# Revit family: NSAL_приток
name_source: partatom
category: Воздухораспределители
revit_build: Autodesk Revit 2014 (Build: 20130308_1515(x64)
units: mm (PartAtom-declared; Revit-internal decimal feet)

## types (144) — shared parameters
1 секция = Да
Offset = 15 мм
T' = 20 мм
URL = http://inplast.ru
Изготовитель = INPLAST-SMAY
Материал = Алюминий_аннодированный (INPLAST)
Рамка_T' = 3 мм
zero-valued in all types: Вес, кг

## per-type parameters (varying)
| type | 2 секция | 3 секция | 4 секция | Aef | L' | W1 | W2 | Вид диффузора | Количество щелей | Описание | Рамка верх | Рамка низ | Тип крепежа |
| NSAL-1-500-0-0-АА | Нет | Нет | Нет | 0.008 м² | 500 мм | 27 мм | 27 мм | единичная установка | 1 | Приточный диффузор однощелевой. Исполнение - алюминий анодированный | Да | Да | с помощью консоли |
| NSAL-2-500-0-0-AA | Да | Нет | Нет | 0.015 м² | 500 мм | 52 мм | 26 мм | единичная установка | 2 | Приточный диффузор двухщелевой. Исполнение - алюминий анодированный | Да | Да | с помощью консоли |
| NSAL-3-500-0-0-AA | Да | Да | Нет | 0.023 м² | 500 мм | 76 мм | 25 мм | единичная установка | 3 | Приточный диффузор трехщелевой. Исполнение - алюминий анодированный | Да | Да | с помощью консоли |
| NSAL-4-500-0-0-AA | Да | Да | Да | 0.030 м² | 500 мм | 101 мм | 25 мм | единичная установка | 4 | Приточный диффузор четырехщелевой. Исполнение - алюминий анодированный | Да | Да | с помощью консоли |
| NSAL-1-500-SK-0-AA | Нет | Нет | Нет | 0.008 м² | 500 мм | 27 мм | 27 мм | крайний элемент | 1 | Приточный диффузор однощелевой. Исполнение - алюминий анодированный | Да | Нет | с помощью консоли |
| NSAL-2-500-SK-0-AA | Да | Нет | Нет | 0.015 м² | 500 мм | 52 мм | 26 мм | крайний элемент | 2 | Приточный диффузор двухщелевой. Исполнение - алюминий анодированный | Да | Нет | с помощью консоли |
| NSAL-3-500-SK-0-AA | Да | Да | Нет | 0.023 м² | 500 мм | 76 мм | 25 мм | крайний элемент | 3 | Приточный диффузор трехщелевой. Исполнение - алюминий анодированный | Да | Нет | с помощью консоли |
| NSAL-4-500-SK-0-AA | Да | Да | Да | 0.030 м² | 500 мм | 101 мм | 25 мм | крайний элемент | 4 | Приточный диффузор четырехщелевой. Исполнение - алюминий анодированный | Да | Нет | с помощью консоли |
| NSAL-1-500-WN-0-AA | Нет | Нет | Нет | 0.008 м² | 500 мм | 27 мм | 27 мм | внутренний элемент | 1 | Приточный диффузор однощелевой. Исполнение - алюминий анодированный | Нет | Нет | с помощью консоли |
| NSAL-2-500-WN-0-AA | Да | Нет | Нет | 0.015 м² | 500 мм | 52 мм | 26 мм | внутренний элемент | 2 | Приточный диффузор двухщелевой. Исполнение - алюминий анодированный | Нет | Нет | с помощью консоли |
| NSAL-3-500-WN-0-AA | Да | Да | Нет | 0.023 м² | 500 мм | 76 мм | 25 мм | внутренний элемент | 3 | Приточный диффузор трехщелевой. Исполнение - алюминий анодированный | Нет | Нет | с помощью консоли |
| NSAL-4-500-WN-0-AA | Да | Да | Да | 0.030 м² | 500 мм | 101 мм | 25 мм | внутренний элемент | 4 | Приточный диффузор четырехщелевой. Исполнение - алюминий анодированный | Нет | Нет | с помощью консоли |
| NSAL-1-500-0-WK-AA | Нет | Нет | Нет | 0.008 м² | 500 мм | 27 мм | 27 мм | единичная установка | 1 | Приточный диффузор однощелевой. Исполнение - алюминий анодированный | Да | Да | с помощью саморезов |
| NSAL-2-500-0-WK-AA | Да | Нет | Нет | 0.015 м² | 500 мм | 52 мм | 26 мм | единичная установка | 2 | Приточный диффузор двухщелевой. Исполнение - алюминий анодированный | Да | Да | с помощью саморезов |
| NSAL-3-500-0-WK-AA | Да | Да | Нет | 0.023 м² | 500 мм | 76 мм | 25 мм | единичная установка | 3 | Приточный диффузор трехщелевой. Исполнение - алюминий анодированный | Да | Да | с помощью саморезов |
| NSAL-4-500-0-WK-AA | Да | Да | Да | 0.030 м² | 500 мм | 101 мм | 25 мм | единичная установка | 4 | Приточный диффузор четырехщелевой. Исполнение - алюминий анодированный | Да | Да | с помощью саморезов |
| NSAL-1-500-SK-WK-AA | Нет | Нет | Нет | 0.008 м² | 500 мм | 27 мм | 27 мм | крайний элемент | 1 | Приточный диффузор однощелевой. Исполнение - алюминий анодированный | Да | Нет | с помощью саморезов |
| NSAL-2-500-SK-WK-AA | Да | Нет | Нет | 0.015 м² | 500 мм | 52 мм | 26 мм | крайний элемент | 2 | Приточный диффузор двухщелевой. Исполнение - алюминий анодированный | Да | Нет | с помощью саморезов |
| NSAL-3-500-SK-WK-AA | Да | Да | Нет | 0.023 м² | 500 мм | 76 мм | 25 мм | крайний элемент | 3 | Приточный диффузор трехщелевой. Исполнение - алюминий анодированный | Да | Нет | с помощью саморезов |
| NSAL-4-500-SK-WK-AA | Да | Да | Да | 0.030 м² | 500 мм | 101 мм | 25 мм | крайний элемент | 4 | Приточный диффузор четырехщелевой. Исполнение - алюминий анодированный | Да | Нет | с помощью саморезов |
| NSAL-1-500-WN-WK-AA | Нет | Нет | Нет | 0.008 м² | 500 мм | 27 мм | 27 мм | внутренний элемент | 1 | Приточный диффузор однощелевой. Исполнение - алюминий анодированный | Нет | Нет | с помощью саморезов |
| NSAL-2-500-WN-WK-AA | Да | Нет | Нет | 0.015 м² | 500 мм | 52 мм | 26 мм | внутренний элемент | 2 | Приточный диффузор двухщелевой. Исполнение - алюминий анодированный | Нет | Нет | с помощью саморезов |
| NSAL-3-500-WN-WK-AA | Да | Да | Нет | 0.023 м² | 500 мм | 76 мм | 25 мм | внутренний элемент | 3 | Приточный диффузор трехщелевой. Исполнение - алюминий анодированный | Нет | Нет | с помощью саморезов |
| NSAL-4-500-WN-WK-AA | Да | Да | Да | 0.030 м² | 500 мм | 101 мм | 25 мм | внутренний элемент | 4 | Приточный диффузор четырехщелевой. Исполнение - алюминий анодированный | Нет | Нет | с помощью саморезов |
| NSAL-1-800-0-0-AA | Нет | Нет | Нет | 0.013 м² | 800 мм | 27 мм | 27 мм | единичная установка | 1 | Приточный диффузор однощелевой. Исполнение - алюминий анодированный | Да | Да | с помощью консоли |
| NSAL-2-800-0-0-AA | Да | Нет | Нет | 0.025 м² | 800 мм | 52 мм | 26 мм | единичная установка | 2 | Приточный диффузор двухщелевой. Исполнение - алюминий анодированный | Да | Да | с помощью консоли |
| NSAL-3-800-0-0-AA | Да | Да | Нет | 0.037 м² | 800 мм | 76 мм | 25 мм | единичная установка | 3 | Приточный диффузор трехщелевой. Исполнение - алюминий анодированный | Да | Да | с помощью консоли |
| NSAL-4-800-0-0-AA | Да | Да | Да | 0.049 м² | 800 мм | 101 мм | 25 мм | единичная установка | 4 | Приточный диффузор четырехщелевой. Исполнение - алюминий анодированный | Да | Да | с помощью консоли |
| NSAL-1-800-SK-0-AA | Нет | Нет | Нет | 0.013 м² | 800 мм | 27 мм | 27 мм | крайний элемент | 1 | Приточный диффузор однощелевой. Исполнение - алюминий анодированный | Да | Нет | с помощью консоли |
| NSAL-2-800-SK-0-AA | Да | Нет | Нет | 0.025 м² | 800 мм | 52 мм | 26 мм | крайний элемент | 2 | Приточный диффузор двухщелевой. Исполнение - алюминий анодированный | Да | Нет | с помощью консоли |
| NSAL-3-800-SK-0-AA | Да | Да | Нет | 0.037 м² | 800 мм | 76 мм | 25 мм | крайний элемент | 3 | Приточный диффузор трехщелевой. Исполнение - алюминий анодированный | Да | Нет | с помощью консоли |
| NSAL-4-800-SK-0-AA | Да | Да | Да | 0.049 м² | 800 мм | 101 мм | 25 мм | крайний элемент | 4 | Приточный диффузор четырехщелевой. Исполнение - алюминий анодированный | Да | Нет | с помощью консоли |
| NSAL-1-800-WN-0-AA | Нет | Нет | Нет | 0.013 м² | 800 мм | 27 мм | 27 мм | внутренний элемент | 1 | Приточный диффузор однощелевой. Исполнение - алюминий анодированный | Нет | Нет | с помощью консоли |
| NSAL-2-800-WN-0-AA | Да | Нет | Нет | 0.025 м² | 800 мм | 52 мм | 26 мм | внутренний элемент | 2 | Приточный диффузор двухщелевой. Исполнение - алюминий анодированный | Нет | Нет | с помощью консоли |
| NSAL-3-800-WN-0-AA | Да | Да | Нет | 0.037 м² | 800 мм | 76 мм | 25 мм | внутренний элемент | 3 | Приточный диффузор трехщелевой. Исполнение - алюминий анодированный | Нет | Нет | с помощью консоли |
| NSAL-4-800-WN-0-AA | Да | Да | Да | 0.049 м² | 800 мм | 101 мм | 25 мм | внутренний элемент | 4 | Приточный диффузор четырехщелевой. Исполнение - алюминий анодированный | Нет | Нет | с помощью консоли |
| NSAL-1-800-0-WK-AA | Нет | Нет | Нет | 0.013 м² | 800 мм | 27 мм | 27 мм | единичная установка | 1 | Приточный диффузор однощелевой. Исполнение - алюминий анодированный | Да | Да | с помощью саморезов |
| NSAL-2-800-0-WK-AA | Да | Нет | Нет | 0.025 м² | 800 мм | 52 мм | 26 мм | единичная установка | 2 | Приточный диффузор двухщелевой. Исполнение - алюминий анодированный | Да | Да | с помощью саморезов |
| NSAL-3-800-0-WK-AA | Да | Да | Нет | 0.037 м² | 800 мм | 76 мм | 25 мм | единичная установка | 3 | Приточный диффузор трехщелевой. Исполнение - алюминий анодированный | Да | Да | с помощью саморезов |
| NSAL-4-800-0-WK-AA | Да | Да | Да | 0.049 м² | 800 мм | 101 мм | 25 мм | единичная установка | 4 | Приточный диффузор четырехщелевой. Исполнение - алюминий анодированный | Да | Да | с помощью саморезов |
| NSAL-1-800-SK-WK-AA | Нет | Нет | Нет | 0.013 м² | 800 мм | 27 мм | 27 мм | крайний элемент | 1 | Приточный диффузор однощелевой. Исполнение - алюминий анодированный | Да | Нет | с помощью саморезов |
| NSAL-2-800-SK-WK-AA | Да | Нет | Нет | 0.025 м² | 800 мм | 52 мм | 26 мм | крайний элемент | 2 | Приточный диффузор двухщелевой. Исполнение - алюминий анодированный | Да | Нет | с помощью саморезов |
| NSAL-3-800-SK-WK-AA | Да | Да | Нет | 0.037 м² | 800 мм | 76 мм | 25 мм | крайний элемент | 3 | Приточный диффузор трехщелевой. Исполнение - алюминий анодированный | Да | Нет | с помощью саморезов |
| NSAL-4-800-SK-WK-AA | Да | Да | Да | 0.049 м² | 800 мм | 101 мм | 25 мм | крайний элемент | 4 | Приточный диффузор четырехщелевой. Исполнение - алюминий анодированный | Да | Нет | с помощью саморезов |
| NSAL-1-800-WN-WK-AA | Нет | Нет | Нет | 0.013 м² | 800 мм | 27 мм | 27 мм | внутренний элемент | 1 | Приточный диффузор однощелевой. Исполнение - алюминий анодированный | Нет | Нет | с помощью саморезов |
| NSAL-2-800-WN-WK-AA | Да | Нет | Нет | 0.025 м² | 800 мм | 52 мм | 26 мм | внутренний элемент | 2 | Приточный диффузор двухщелевой. Исполнение - алюминий анодированный | Нет | Нет | с помощью саморезов |
| NSAL-3-800-WN-WK-AA | Да | Да | Нет | 0.037 м² | 800 мм | 76 мм | 25 мм | внутренний элемент | 3 | Приточный диффузор трехщелевой. Исполнение - алюминий анодированный | Нет | Нет | с помощью саморезов |
| NSAL-4-800-WN-WK-AA | Да | Да | Да | 0.049 м² | 800 мм | 101 мм | 25 мм | внутренний элемент | 4 | Приточный диффузор четырехщелевой. Исполнение - алюминий анодированный | Нет | Нет | с помощью саморезов |
| NSAL-1-1000-0-0-AA | Нет | Нет | Нет | 0.016 м² | 1000 мм | 27 мм | 27 мм | единичная установка | 1 | Приточный диффузор однощелевой. Исполнение - алюминий анодированный | Да | Да | с помощью консоли |
| NSAL-2-1000-0-0-AA | Да | Нет | Нет | 0.031 м² | 1000 мм | 52 мм | 26 мм | единичная установка | 2 | Приточный диффузор двухщелевой. Исполнение - алюминий анодированный | Да | Да | с помощью консоли |
| NSAL-3-1000-0-0-AA | Да | Да | Нет | 0.046 м² | 1000 мм | 76 мм | 25 мм | единичная установка | 3 | Приточный диффузор трехщелевой. Исполнение - алюминий анодированный | Да | Да | с помощью консоли |
| NSAL-4-1000-0-0-AA | Да | Да | Да | 0.061 м² | 1000 мм | 101 мм | 25 мм | единичная установка | 4 | Приточный диффузор четырехщелевой. Исполнение - алюминий анодированный | Да | Да | с помощью консоли |
| NSAL-1-1000-SK-0-AA | Нет | Нет | Нет | 0.016 м² | 1000 мм | 27 мм | 27 мм | крайний элемент | 1 | Приточный диффузор однощелевой. Исполнение - алюминий анодированный | Да | Нет | с помощью консоли |
| NSAL-2-1000-SK-0-AA | Да | Нет | Нет | 0.031 м² | 1000 мм | 52 мм | 26 мм | крайний элемент | 2 | Приточный диффузор двухщелевой. Исполнение - алюминий анодированный | Да | Нет | с помощью консоли |
| NSAL-3-1000-SK-0-AA | Да | Да | Нет | 0.046 м² | 1000 мм | 76 мм | 25 мм | крайний элемент | 3 | Приточный диффузор трехщелевой. Исполнение - алюминий анодированный | Да | Нет | с помощью консоли |
| NSAL-4-1000-SK-0-AA | Да | Да | Да | 0.061 м² | 1000 мм | 101 мм | 25 мм | крайний элемент | 4 | Приточный диффузор четырехщелевой. Исполнение - алюминий анодированный | Да | Нет | с помощью консоли |
| NSAL-1-1000-WN-0-AA | Нет | Нет | Нет | 0.016 м² | 1000 мм | 27 мм | 27 мм | внутренний элемент | 1 | Приточный диффузор однощелевой. Исполнение - алюминий анодированный | Нет | Нет | с помощью консоли |
| NSAL-2-1000-WN-0-AA | Да | Нет | Нет | 0.031 м² | 1000 мм | 52 мм | 26 мм | внутренний элемент | 2 | Приточный диффузор двухщелевой. Исполнение - алюминий анодированный | Нет | Нет | с помощью консоли |
| NSAL-3-1000-WN-0-AA | Да | Да | Нет | 0.046 м² | 1000 мм | 76 мм | 25 мм | внутренний элемент | 3 | Приточный диффузор трехщелевой. Исполнение - алюминий анодированный | Нет | Нет | с помощью консоли |
| NSAL-4-1000-WN-0-AA | Да | Да | Да | 0.061 м² | 1000 мм | 101 мм | 25 мм | внутренний элемент | 4 | Приточный диффузор четырехщелевой. Исполнение - алюминий анодированный | Нет | Нет | с помощью консоли |
| NSAL-1-1000-0-WK-AA | Нет | Нет | Нет | 0.016 м² | 1000 мм | 27 мм | 27 мм | единичная установка | 1 | Приточный диффузор однощелевой. Исполнение - алюминий анодированный | Да | Да | с помощью саморезов |
| NSAL-2-1000-0-WK-AA | Да | Нет | Нет | 0.031 м² | 1000 мм | 52 мм | 26 мм | единичная установка | 2 | Приточный диффузор двухщелевой. Исполнение - алюминий анодированный | Да | Да | с помощью саморезов |
| NSAL-3-1000-0-WK-AA | Да | Да | Нет | 0.046 м² | 1000 мм | 76 мм | 25 мм | единичная установка | 3 | Приточный диффузор трехщелевой. Исполнение - алюминий анодированный | Да | Да | с помощью саморезов |
| NSAL-4-1000-0-WK-AA | Да | Да | Да | 0.061 м² | 1000 мм | 101 мм | 25 мм | единичная установка | 4 | Приточный диффузор четырехщелевой. Исполнение - алюминий анодированный | Да | Да | с помощью саморезов |
| NSAL-1-1000-SK-WK-AA | Нет | Нет | Нет | 0.016 м² | 1000 мм | 27 мм | 27 мм | крайний элемент | 1 | Приточный диффузор однощелевой. Исполнение - алюминий анодированный | Да | Нет | с помощью саморезов |
| NSAL-2-1000-SK-WK-AA | Да | Нет | Нет | 0.031 м² | 1000 мм | 52 мм | 26 мм | крайний элемент | 2 | Приточный диффузор двухщелевой. Исполнение - алюминий анодированный | Да | Нет | с помощью саморезов |
| NSAL-3-1000-SK-WK-AA | Да | Да | Нет | 0.046 м² | 1000 мм | 76 мм | 25 мм | крайний элемент | 3 | Приточный диффузор трехщелевой. Исполнение - алюминий анодированный | Да | Нет | с помощью саморезов |
| NSAL-4-1000-SK-WK-AA | Да | Да | Да | 0.061 м² | 1000 мм | 101 мм | 25 мм | крайний элемент | 4 | Приточный диффузор четырехщелевой. Исполнение - алюминий анодированный | Да | Нет | с помощью саморезов |
| NSAL-1-1000-WN-WK-AA | Нет | Нет | Нет | 0.016 м² | 1000 мм | 27 мм | 27 мм | внутренний элемент | 1 | Приточный диффузор однощелевой. Исполнение - алюминий анодированный | Нет | Нет | с помощью саморезов |
| NSAL-2-1000-WN-WK-AA | Да | Нет | Нет | 0.031 м² | 1000 мм | 52 мм | 26 мм | внутренний элемент | 2 | Приточный диффузор двухщелевой. Исполнение - алюминий анодированный | Нет | Нет | с помощью саморезов |
| NSAL-3-1000-WN-WK-AA | Да | Да | Нет | 0.046 м² | 1000 мм | 76 мм | 25 мм | внутренний элемент | 3 | Приточный диффузор трехщелевой. Исполнение - алюминий анодированный | Нет | Нет | с помощью саморезов |
| NSAL-4-1000-WN-WK-AA | Да | Да | Да | 0.061 м² | 1000 мм | 101 мм | 25 мм | внутренний элемент | 4 | Приточный диффузор четырехщелевой. Исполнение - алюминий анодированный | Нет | Нет | с помощью саморезов |
| NSAL-1-1200-0-0-AA | Нет | Нет | Нет | 0.019 м² | 1200 мм | 27 мм | 27 мм | единичная установка | 1 | Приточный диффузор однощелевой. Исполнение - алюминий анодированный | Да | Да | с помощью консоли |
| NSAL-2-1200-0-0-AA | Да | Нет | Нет | 0.037 м² | 1200 мм | 52 мм | 26 мм | единичная установка | 2 | Приточный диффузор двухщелевой. Исполнение - алюминий анодированный | Да | Да | с помощью консоли |
| NSAL-3-1200-0-0-AA | Да | Да | Нет | 0.055 м² | 1200 мм | 76 мм | 25 мм | единичная установка | 3 | Приточный диффузор трехщелевой. Исполнение - алюминий анодированный | Да | Да | с помощью консоли |
| NSAL-4-1200-0-0-AA | Да | Да | Да | 0.073 м² | 1200 мм | 101 мм | 25 мм | единичная установка | 4 | Приточный диффузор четырехщелевой. Исполнение - алюминий анодированный | Да | Да | с помощью консоли |
| NSAL-1-1200-SK-0-AA | Нет | Нет | Нет | 0.019 м² | 1200 мм | 27 мм | 27 мм | крайний элемент | 1 | Приточный диффузор однощелевой. Исполнение - алюминий анодированный | Да | Нет | с помощью консоли |
| NSAL-2-1200-SK-0-AA | Да | Нет | Нет | 0.037 м² | 1200 мм | 52 мм | 26 мм | крайний элемент | 2 | Приточный диффузор двухщелевой. Исполнение - алюминий анодированный | Да | Нет | с помощью консоли |
| NSAL-3-1200-SK-0-AA | Да | Да | Нет | 0.055 м² | 1200 мм | 76 мм | 25 мм | крайний элемент | 3 | Приточный диффузор трехщелевой. Исполнение - алюминий анодированный | Да | Нет | с помощью консоли |
| NSAL-4-1200-SK-0-AA | Да | Да | Да | 0.073 м² | 1200 мм | 101 мм | 25 мм | крайний элемент | 4 | Приточный диффузор четырехщелевой. Исполнение - алюминий анодированный | Да | Нет | с помощью консоли |
| NSAL-1-1200-WN-0-AA | Нет | Нет | Нет | 0.019 м² | 1200 мм | 27 мм | 27 мм | внутренний элемент | 1 | Приточный диффузор однощелевой. Исполнение - алюминий анодированный | Нет | Нет | с помощью консоли |
| NSAL-2-1200-WN-0-AA | Да | Нет | Нет | 0.037 м² | 1200 мм | 52 мм | 26 мм | внутренний элемент | 2 | Приточный диффузор двухщелевой. Исполнение - алюминий анодированный | Нет | Нет | с помощью консоли |
| NSAL-3-1200-WN-0-AA | Да | Да | Нет | 0.055 м² | 1200 мм | 76 мм | 25 мм | внутренний элемент | 3 | Приточный диффузор трехщелевой. Исполнение - алюминий анодированный | Нет | Нет | с помощью консоли |
| NSAL-4-1200-WN-0-AA | Да | Да | Да | 0.073 м² | 1200 мм | 101 мм | 25 мм | внутренний элемент | 4 | Приточный диффузор четырехщелевой. Исполнение - алюминий анодированный | Нет | Нет | с помощью консоли |
| NSAL-1-1200-0-WK-AA | Нет | Нет | Нет | 0.019 м² | 1200 мм | 27 мм | 27 мм | единичная установка | 1 | Приточный диффузор однощелевой. Исполнение - алюминий анодированный | Да | Да | с помощью саморезов |
| NSAL-2-1200-0-WK-AA | Да | Нет | Нет | 0.037 м² | 1200 мм | 52 мм | 26 мм | единичная установка | 2 | Приточный диффузор двухщелевой. Исполнение - алюминий анодированный | Да | Да | с помощью саморезов |
| NSAL-3-1200-0-WK-AA | Да | Да | Нет | 0.055 м² | 1200 мм | 76 мм | 25 мм | единичная установка | 3 | Приточный диффузор трехщелевой. Исполнение - алюминий анодированный | Да | Да | с помощью саморезов |
| NSAL-4-1200-0-WK-AA | Да | Да | Да | 0.073 м² | 1200 мм | 101 мм | 25 мм | единичная установка | 4 | Приточный диффузор четырехщелевой. Исполнение - алюминий анодированный | Да | Да | с помощью саморезов |
| NSAL-1-1200-SK-WK-AA | Нет | Нет | Нет | 0.019 м² | 1200 мм | 27 мм | 27 мм | крайний элемент | 1 | Приточный диффузор однощелевой. Исполнение - алюминий анодированный | Да | Нет | с помощью саморезов |
| NSAL-2-1200-SK-WK-AA | Да | Нет | Нет | 0.037 м² | 1200 мм | 52 мм | 26 мм | крайний элемент | 2 | Приточный диффузор двухщелевой. Исполнение - алюминий анодированный | Да | Нет | с помощью саморезов |
| NSAL-3-1200-SK-WK-AA | Да | Да | Нет | 0.055 м² | 1200 мм | 76 мм | 25 мм | крайний элемент | 3 | Приточный диффузор трехщелевой. Исполнение - алюминий анодированный | Да | Нет | с помощью саморезов |
| NSAL-4-1200-SK-WK-AA | Да | Да | Да | 0.073 м² | 1200 мм | 101 мм | 25 мм | крайний элемент | 4 | Приточный диффузор четырехщелевой. Исполнение - алюминий анодированный | Да | Нет | с помощью саморезов |
| NSAL-1-1200-WN-WK-AA | Нет | Нет | Нет | 0.019 м² | 1200 мм | 27 мм | 27 мм | внутренний элемент | 1 | Приточный диффузор однощелевой. Исполнение - алюминий анодированный | Нет | Нет | с помощью саморезов |
| NSAL-2-1200-WN-WK-AA | Да | Нет | Нет | 0.037 м² | 1200 мм | 52 мм | 26 мм | внутренний элемент | 2 | Приточный диффузор двухщелевой. Исполнение - алюминий анодированный | Нет | Нет | с помощью саморезов |
| NSAL-3-1200-WN-WK-AA | Да | Да | Нет | 0.055 м² | 1200 мм | 76 мм | 25 мм | внутренний элемент | 3 | Приточный диффузор трехщелевой. Исполнение - алюминий анодированный | Нет | Нет | с помощью саморезов |
| NSAL-4-1200-WN-WK-AA | Да | Да | Да | 0.073 м² | 1200 мм | 101 мм | 25 мм | внутренний элемент | 4 | Приточный диффузор четырехщелевой. Исполнение - алюминий анодированный | Нет | Нет | с помощью саморезов |
| NSAL-1-1500-0-0-AA | Нет | Нет | Нет | 0.024 м² | 1500 мм | 27 мм | 27 мм | единичная установка | 1 | Приточный диффузор однощелевой. Исполнение - алюминий анодированный | Да | Да | с помощью консоли |
| NSAL-2-1500-0-0-AA | Да | Нет | Нет | 0.046 м² | 1500 мм | 52 мм | 26 мм | единичная установка | 2 | Приточный диффузор двухщелевой. Исполнение - алюминий анодированный | Да | Да | с помощью консоли |
| NSAL-3-1500-0-0-AA | Да | Да | Нет | 0.069 м² | 1500 мм | 76 мм | 25 мм | единичная установка | 3 | Приточный диффузор трехщелевой. Исполнение - алюминий анодированный | Да | Да | с помощью консоли |
| NSAL-4-1500-0-0-AA | Да | Да | Да | 0.091 м² | 1500 мм | 101 мм | 25 мм | единичная установка | 4 | Приточный диффузор четырехщелевой. Исполнение - алюминий анодированный | Да | Да | с помощью консоли |
| NSAL-1-1500-SK-0-AA | Нет | Нет | Нет | 0.024 м² | 1500 мм | 27 мм | 27 мм | крайний элемент | 1 | Приточный диффузор однощелевой. Исполнение - алюминий анодированный | Да | Нет | с помощью консоли |
| NSAL-2-1500-SK-0-AA | Да | Нет | Нет | 0.046 м² | 1500 мм | 52 мм | 26 мм | крайний элемент | 2 | Приточный диффузор двухщелевой. Исполнение - алюминий анодированный | Да | Нет | с помощью консоли |
| NSAL-3-1500-SK-0-AA | Да | Да | Нет | 0.069 м² | 1500 мм | 76 мм | 25 мм | крайний элемент | 3 | Приточный диффузор трехщелевой. Исполнение - алюминий анодированный | Да | Нет | с помощью консоли |
| NSAL-4-1500-SK-0-AA | Да | Да | Да | 0.091 м² | 1500 мм | 101 мм | 25 мм | крайний элемент | 4 | Приточный диффузор четырехщелевой. Исполнение - алюминий анодированный | Да | Нет | с помощью консоли |
| NSAL-1-1500-WN-0-AA | Нет | Нет | Нет | 0.024 м² | 1500 мм | 27 мм | 27 мм | внутренний элемент | 1 | Приточный диффузор однощелевой. Исполнение - алюминий анодированный | Нет | Нет | с помощью консоли |
| NSAL-2-1500-WN-0-AA | Да | Нет | Нет | 0.046 м² | 1500 мм | 52 мм | 26 мм | внутренний элемент | 2 | Приточный диффузор двухщелевой. Исполнение - алюминий анодированный | Нет | Нет | с помощью консоли |
| NSAL-3-1500-WN-0-AA | Да | Да | Нет | 0.069 м² | 1500 мм | 76 мм | 25 мм | внутренний элемент | 3 | Приточный диффузор трехщелевой. Исполнение - алюминий анодированный | Нет | Нет | с помощью консоли |
| NSAL-4-1500-WN-0-AA | Да | Да | Да | 0.091 м² | 1500 мм | 101 мм | 25 мм | внутренний элемент | 4 | Приточный диффузор четырехщелевой. Исполнение - алюминий анодированный | Нет | Нет | с помощью консоли |
| NSAL-1-1500-0-WK-AA | Нет | Нет | Нет | 0.024 м² | 1500 мм | 27 мм | 27 мм | единичная установка | 1 | Приточный диффузор однощелевой. Исполнение - алюминий анодированный | Да | Да | с помощью саморезов |
| NSAL-2-1500-0-WK-AA | Да | Нет | Нет | 0.046 м² | 1500 мм | 52 мм | 26 мм | единичная установка | 2 | Приточный диффузор двухщелевой. Исполнение - алюминий анодированный | Да | Да | с помощью саморезов |
| NSAL-3-1500-0-WK-AA | Да | Да | Нет | 0.069 м² | 1500 мм | 76 мм | 25 мм | единичная установка | 3 | Приточный диффузор трехщелевой. Исполнение - алюминий анодированный | Да | Да | с помощью саморезов |
| NSAL-4-1500-0-WK-AA | Да | Да | Да | 0.091 м² | 1500 мм | 101 мм | 25 мм | единичная установка | 4 | Приточный диффузор четырехщелевой. Исполнение - алюминий анодированный | Да | Да | с помощью саморезов |
| NSAL-1-1500-SK-WK-AA | Нет | Нет | Нет | 0.024 м² | 1500 мм | 27 мм | 27 мм | крайний элемент | 1 | Приточный диффузор однощелевой. Исполнение - алюминий анодированный | Да | Нет | с помощью саморезов |
| NSAL-2-1500-SK-WK-AA | Да | Нет | Нет | 0.046 м² | 1500 мм | 52 мм | 26 мм | крайний элемент | 2 | Приточный диффузор двухщелевой. Исполнение - алюминий анодированный | Да | Нет | с помощью саморезов |
| NSAL-3-1500-SK-WK-AA | Да | Да | Нет | 0.069 м² | 1500 мм | 76 мм | 25 мм | крайний элемент | 3 | Приточный диффузор трехщелевой. Исполнение - алюминий анодированный | Да | Нет | с помощью саморезов |
| NSAL-4-1500-SK-WK-AA | Да | Да | Да | 0.091 м² | 1500 мм | 101 мм | 25 мм | крайний элемент | 4 | Приточный диффузор четырехщелевой. Исполнение - алюминий анодированный | Да | Нет | с помощью саморезов |
| NSAL-1-1500-WN-WK-AA | Нет | Нет | Нет | 0.024 м² | 1500 мм | 27 мм | 27 мм | внутренний элемент | 1 | Приточный диффузор однощелевой. Исполнение - алюминий анодированный | Нет | Нет | с помощью саморезов |
| NSAL-2-1500-WN-WK-AA | Да | Нет | Нет | 0.046 м² | 1500 мм | 52 мм | 26 мм | внутренний элемент | 2 | Приточный диффузор двухщелевой. Исполнение - алюминий анодированный | Нет | Нет | с помощью саморезов |
| NSAL-3-1500-WN-WK-AA | Да | Да | Нет | 0.069 м² | 1500 мм | 76 мм | 25 мм | внутренний элемент | 3 | Приточный диффузор трехщелевой. Исполнение - алюминий анодированный | Нет | Нет | с помощью саморезов |
| NSAL-4-1500-WN-WK-AA | Да | Да | Да | 0.091 м² | 1500 мм | 101 мм | 25 мм | внутренний элемент | 4 | Приточный диффузор четырехщелевой. Исполнение - алюминий анодированный | Нет | Нет | с помощью саморезов |
| NSAL-1-2000-0-0-AA | Нет | Нет | Нет | 0.032 м² | 2000 мм | 27 мм | 27 мм | единичная установка | 1 | Приточный диффузор однощелевой. Исполнение - алюминий анодированный | Да | Да | с помощью консоли |
| NSAL-2-2000-0-0-AA | Да | Нет | Нет | 0.062 м² | 2000 мм | 52 мм | 26 мм | единичная установка | 2 | Приточный диффузор двухщелевой. Исполнение - алюминий анодированный | Да | Да | с помощью консоли |
| NSAL-3-2000-0-0-AA | Да | Да | Нет | 0.091 м² | 2000 мм | 76 мм | 25 мм | единичная установка | 3 | Приточный диффузор трехщелевой. Исполнение - алюминий анодированный | Да | Да | с помощью консоли |
| NSAL-4-2000-0-0-AA | Да | Да | Да | 0.122 м² | 2000 мм | 101 мм | 25 мм | единичная установка | 4 | Приточный диффузор четырехщелевой. Исполнение - алюминий анодированный | Да | Да | с помощью консоли |
| NSAL-1-2000-SK-0-AA | Нет | Нет | Нет | 0.032 м² | 2000 мм | 27 мм | 27 мм | крайний элемент | 1 | Приточный диффузор однощелевой. Исполнение - алюминий анодированный | Да | Нет | с помощью консоли |
| NSAL-2-2000-SK-0-AA | Да | Нет | Нет | 0.062 м² | 2000 мм | 52 мм | 26 мм | крайний элемент | 2 | Приточный диффузор двухщелевой. Исполнение - алюминий анодированный | Да | Нет | с помощью консоли |
| NSAL-3-2000-SK-0-AA | Да | Да | Нет | 0.091 м² | 2000 мм | 76 мм | 25 мм | крайний элемент | 3 | Приточный диффузор трехщелевой. Исполнение - алюминий анодированный | Да | Нет | с помощью консоли |
| NSAL-4-2000-SK-0-AA | Да | Да | Да | 0.122 м² | 2000 мм | 101 мм | 25 мм | крайний элемент | 4 | Приточный диффузор четырехщелевой. Исполнение - алюминий анодированный | Да | Нет | с помощью консоли |
| NSAL-1-2000-WN-0-AA | Нет | Нет | Нет | 0.032 м² | 2000 мм | 27 мм | 27 мм | внутренний элемент | 1 | Приточный диффузор однощелевой. Исполнение - алюминий анодированный | Нет | Нет | с помощью консоли |
| NSAL-2-2000-WN-0-AA | Да | Нет | Нет | 0.062 м² | 2000 мм | 52 мм | 26 мм | внутренний элемент | 2 | Приточный диффузор двухщелевой. Исполнение - алюминий анодированный | Нет | Нет | с помощью консоли |
| NSAL-3-2000-WN-0-AA | Да | Да | Нет | 0.091 м² | 2000 мм | 76 мм | 25 мм | внутренний элемент | 3 | Приточный диффузор трехщелевой. Исполнение - алюминий анодированный | Нет | Нет | с помощью консоли |
| NSAL-4-2000-WN-0-AA | Да | Да | Да | 0.122 м² | 2000 мм | 101 мм | 25 мм | внутренний элемент | 4 | Приточный диффузор четырехщелевой. Исполнение - алюминий анодированный | Нет | Нет | с помощью консоли |
| NSAL-1-2000-0-WK-AA | Нет | Нет | Нет | 0.032 м² | 2000 мм | 27 мм | 27 мм | единичная установка | 1 | Приточный диффузор однощелевой. Исполнение - алюминий анодированный | Да | Да | с помощью саморезов |
| NSAL-2-2000-0-WK-AA | Да | Нет | Нет | 0.062 м² | 2000 мм | 52 мм | 26 мм | единичная установка | 2 | Приточный диффузор двухщелевой. Исполнение - алюминий анодированный | Да | Да | с помощью саморезов |
| NSAL-3-2000-0-WK-AA | Да | Да | Нет | 0.091 м² | 2000 мм | 76 мм | 25 мм | единичная установка | 3 | Приточный диффузор трехщелевой. Исполнение - алюминий анодированный | Да | Да | с помощью саморезов |
| NSAL-4-2000-0-WK-AA | Да | Да | Да | 0.122 м² | 2000 мм | 101 мм | 25 мм | единичная установка | 4 | Приточный диффузор четырехщелевой. Исполнение - алюминий анодированный | Да | Да | с помощью саморезов |
| NSAL-1-2000-SK-WK-AA | Нет | Нет | Нет | 0.032 м² | 2000 мм | 27 мм | 27 мм | крайний элемент | 1 | Приточный диффузор однощелевой. Исполнение - алюминий анодированный | Да | Нет | с помощью саморезов |
| NSAL-2-2000-SK-WK-AA | Да | Нет | Нет | 0.062 м² | 2000 мм | 52 мм | 26 мм | крайний элемент | 2 | Приточный диффузор двухщелевой. Исполнение - алюминий анодированный | Да | Нет | с помощью саморезов |
| NSAL-3-2000-SK-WK-AA | Да | Да | Нет | 0.091 м² | 2000 мм | 76 мм | 25 мм | крайний элемент | 3 | Приточный диффузор трехщелевой. Исполнение - алюминий анодированный | Да | Нет | с помощью саморезов |
| NSAL-4-2000-SK-WK-AA | Да | Да | Да | 0.122 м² | 2000 мм | 101 мм | 25 мм | крайний элемент | 4 | Приточный диффузор четырехщелевой. Исполнение - алюминий анодированный | Да | Нет | с помощью саморезов |
| NSAL-1-2000-WN-WK-AA | Нет | Нет | Нет | 0.032 м² | 2000 мм | 27 мм | 27 мм | внутренний элемент | 1 | Приточный диффузор однощелевой. Исполнение - алюминий анодированный | Нет | Нет | с помощью саморезов |
| NSAL-2-2000-WN-WK-AA | Да | Нет | Нет | 0.062 м² | 2000 мм | 52 мм | 26 мм | внутренний элемент | 2 | Приточный диффузор двухщелевой. Исполнение - алюминий анодированный | Нет | Нет | с помощью саморезов |
| NSAL-3-2000-WN-WK-AA | Да | Да | Нет | 0.091 м² | 2000 мм | 76 мм | 25 мм | внутренний элемент | 3 | Приточный диффузор трехщелевой. Исполнение - алюминий анодированный | Нет | Нет | с помощью саморезов |
| NSAL-4-2000-WN-WK-AA | Да | Да | Да | 0.122 м² | 2000 мм | 101 мм | 25 мм | внутренний элемент | 4 | Приточный диффузор четырехщелевой. Исполнение - алюминий анодированный | Нет | Нет | с помощью саморезов |

note: column(s) folded — value = type name in every type: Комментарии к типоразмеру
